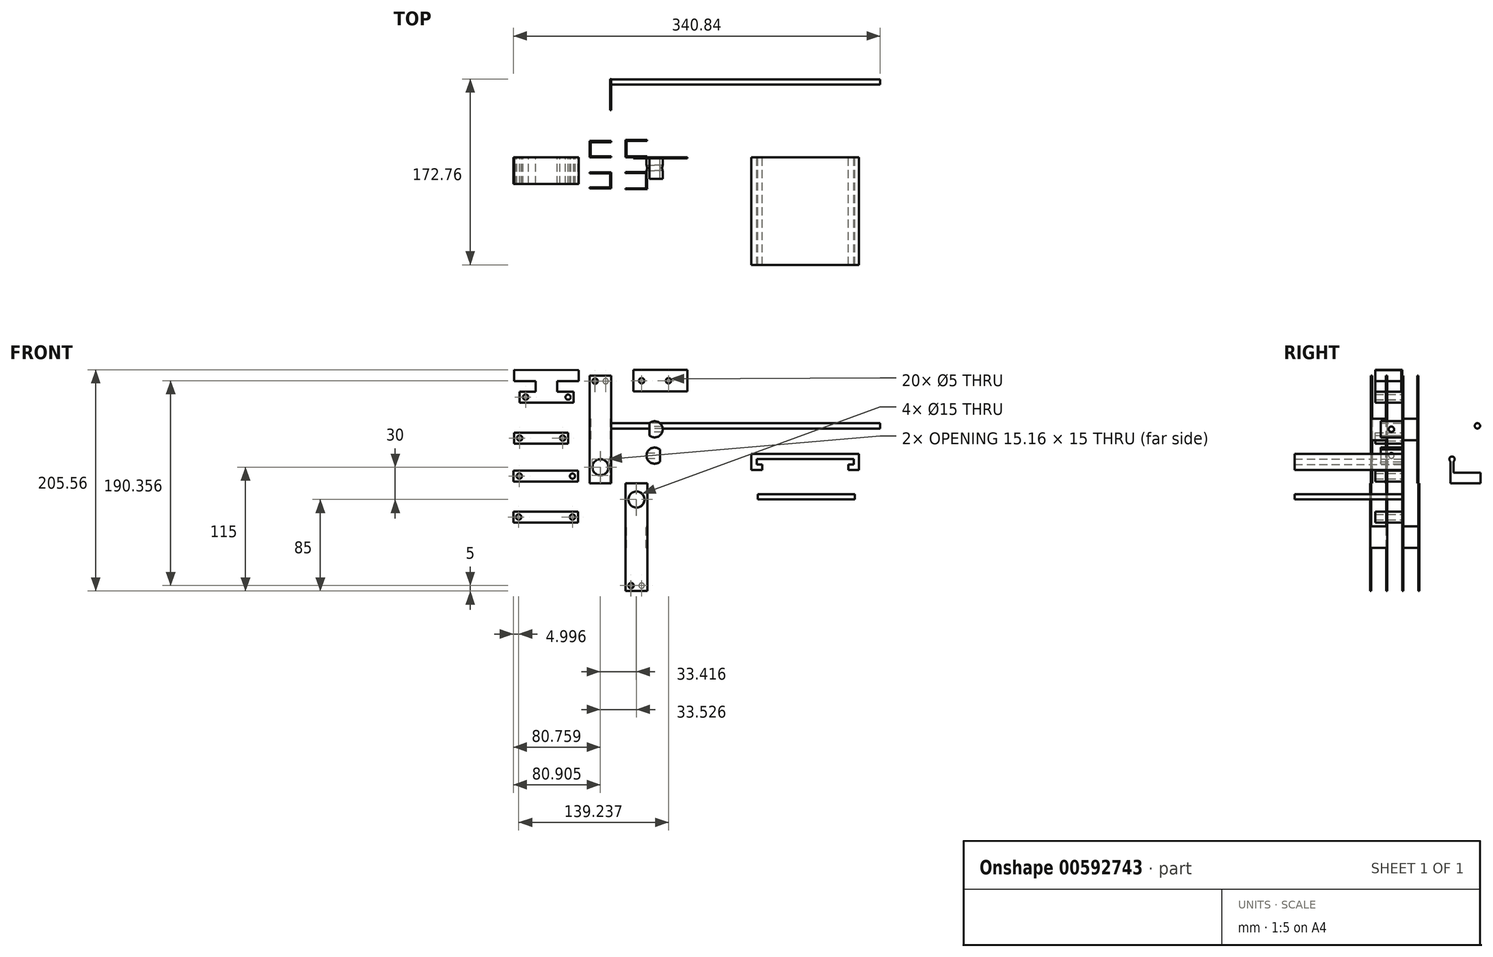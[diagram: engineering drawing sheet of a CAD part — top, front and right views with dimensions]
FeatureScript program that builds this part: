
annotation { "Feature Type Name" : "Feature", "Feature Type Description" : "" }
export const myFeature = defineFeature(function(context is Context, id is Id, definition is map)
    precondition{}
    {
        {
            var Q0;
            Q0=qCreatedBy(makeId("Top.planeOp"),FACE);
            var sketch = newSketch(context, id + "F0", { "sketchPlane" : qUnion([Q0])});
            skLineSegment(sketch, "E0", {"start": v(0, 15) * mm, "end": v(-20, 15) * mm});
            skLineSegment(sketch, "E1", {"start": v(-20, 15) * mm, "end": v(-20, 0) * mm});
            skLineSegment(sketch, "E2", {"start": v(-20, 0) * mm, "end": v(0, 0) * mm});
            skLineSegment(sketch, "E3", {"start": v(0, 0) * mm, "end": v(0, 1) * mm});
            skLineSegment(sketch, "E4", {"start": v(0, 1) * mm, "end": v(-19, 1) * mm});
            skLineSegment(sketch, "E5", {"start": v(-19, 1) * mm, "end": v(-19, 14) * mm});
            skLineSegment(sketch, "E6", {"start": v(-19, 14) * mm, "end": v(0, 14) * mm});
            skLineSegment(sketch, "E7", {"start": v(0, 14) * mm, "end": v(0, 15) * mm});
            skLineSegment(sketch, "E8", {"start": v(33.42, 1) * mm, "end": v(14.42, 1) * mm});
            skLineSegment(sketch, "E9", {"start": v(14.42, 1) * mm, "end": v(14.42, 15) * mm});
            skLineSegment(sketch, "E10", {"start": v(14.42, 15) * mm, "end": v(33.42, 15) * mm});
            skLineSegment(sketch, "E11", {"start": v(33.42, 15) * mm, "end": v(33.42, 16) * mm});
            skLineSegment(sketch, "E12", {"start": v(33.42, 16) * mm, "end": v(13.42, 16) * mm});
            skLineSegment(sketch, "E13", {"start": v(13.42, 16) * mm, "end": v(13.42, 0) * mm});
            skLineSegment(sketch, "E14", {"start": v(13.42, 0) * mm, "end": v(33.42, 0) * mm});
            skLineSegment(sketch, "E15", {"start": v(33.42, 0) * mm, "end": v(33.42, 1) * mm});
            skLineSegment(sketch, "E16", {"start": v(-36.62, -7.13) * mm, "end": v(38.64, -6.85) * mm, "construction": true});
            skLineSegment(sketch, "E17.MirrorCS", {"start": v(-19, 16) * mm, "end": v(0, 16) * mm});
            skLineSegment(sketch, "E18.MirrorCS", {"start": v(-19.95, -14.13) * mm, "end": v(0.05, -13.99) * mm});
            skLineSegment(sketch, "E19.MirrorCS", {"start": v(0.16, -28.99) * mm, "end": v(-19.84, -29.13) * mm});
            skLineSegment(sketch, "E20.MirrorCS", {"start": v(13.47, -13.89) * mm, "end": v(33.47, -13.74) * mm});
            skLineSegment(sketch, "E21.MirrorCS", {"start": v(33.58, -29.74) * mm, "end": v(13.58, -29.89) * mm});
            skLineSegment(sketch, "E22", {"start": v(13.47, -13.89) * mm, "end": v(13.47, -14.89) * mm});
            skLineSegment(sketch, "E23", {"start": v(13.47, -14.89) * mm, "end": v(32.47, -14.75) * mm});
            skLineSegment(sketch, "E24", {"start": v(32.58, -28.75) * mm, "end": v(13.58, -28.89) * mm});
            skLineSegment(sketch, "E25", {"start": v(13.58, -28.89) * mm, "end": v(13.58, -29.89) * mm});
            skLineSegment(sketch, "E26", {"start": v(32.58, -28.75) * mm, "end": v(32.47, -14.75) * mm});
            skLineSegment(sketch, "E27", {"start": v(33.47, -13.74) * mm, "end": v(33.58, -29.74) * mm});
            skLineSegment(sketch, "E28", {"start": v(0.05, -13.99) * mm, "end": v(0.16, -28.99) * mm});
            skLineSegment(sketch, "E29", {"start": v(-19.95, -14.13) * mm, "end": v(-19.94, -15.13) * mm});
            skLineSegment(sketch, "E30", {"start": v(-19.94, -15.13) * mm, "end": v(-0.94, -15) * mm});
            skLineSegment(sketch, "E31", {"start": v(-0.94, -15) * mm, "end": v(-0.85, -28) * mm});
            skLineSegment(sketch, "E32", {"start": v(-0.85, -28) * mm, "end": v(-19.84, -28.13) * mm});
            skLineSegment(sketch, "E33", {"start": v(-19.84, -29.13) * mm, "end": v(-19.84, -28.13) * mm});
            skSolve(sketch);
        }
        {
            var Q0;
            Q0=makeQuery(id+"F0.imprint","IMPRINT",FACE,{"disambiguationData":[TD([[makeQuery(id+"F0.imprint","IMPRINT",EDGE,{"derivedFrom":sQuery(id+"F0.wireOp",EDGE,"E0")}),1.0]])]});
            var Q1;
            Q1=makeQuery(id+"F0.imprint","IMPRINT",FACE,{"disambiguationData":[TD([[makeQuery(id+"F0.imprint","IMPRINT",EDGE,{"derivedFrom":sQuery(id+"F0.wireOp",EDGE,"E19.MirrorCS")}),-1.0]])]});
            extrude(context, id + "F1", {"entities" : qUnion([Q0, Q1]), "depth" : 100 * mm, "offsetDistance" : 25 * mm});
        }
        {
            var Q0;
            Q0=makeQuery(id+"F1.opExtrude","SWEPT_FACE",FACE,{"disambiguationData":[OSD([sQuery(id+"F0.wireOp",EDGE,"E2")])]});
            var sketch = newSketch(context, id + "F2", { "sketchPlane" : qUnion([Q0])});
            skCircle(sketch, "E34", {"center": v(-10, 15) * mm, "radius": 7.5 * mm});
            skPoint(sketch, "E34.centerSnap0", {"position": v(-10, 0) * mm});
            skCircle(sketch, "E35", {"center": v(-5, 95) * mm, "radius": 2.5 * mm});
            skSolve(sketch);
        }
        {
            var Q0;
            Q0=makeQuery(id+"F2.imprint","IMPRINT",FACE,{"disambiguationData":[TD([[makeQuery(id+"F2.imprint","IMPRINT",EDGE,{"derivedFrom":sQuery(id+"F2.wireOp",EDGE,"E34")}),1.0]])]});
            var Q1;
            Q1=makeQuery(id+"F2.imprint","IMPRINT",FACE,{"disambiguationData":[TD([[makeQuery(id+"F2.imprint","IMPRINT",EDGE,{"derivedFrom":sQuery(id+"F2.wireOp",EDGE,"E35")}),1.0]])]});
            extrude(context, id + "F3", {"entities" : qUnion([Q0, Q1]), "operationType" : NewBodyOperationType.REMOVE, "endBound" : BoundingType.THROUGH_ALL, "oppositeDirection" : true, "depth" : 25 * mm, "offsetDistance" : 25 * mm});
        }
        {
            var Q0;
            Q0=makeQuery(id+"F1.opExtrude","SWEPT_FACE",FACE,{"disambiguationData":[OSD([sQuery(id+"F0.wireOp",EDGE,"E1")])]});
            var sketch = newSketch(context, id + "F4", { "sketchPlane" : qUnion([Q0])});
            skPoint(sketch, "E36.centerSnap0", {"position": v(-7.5, 0) * mm});
            skLineSegment(sketch, "E37", {"start": v(-14, 0) * mm, "end": v(-14, 40) * mm});
            skLineSegment(sketch, "E38", {"start": v(-14, 40) * mm, "end": v(-1, 40) * mm});
            skLineSegment(sketch, "E39", {"start": v(-1, 40) * mm, "end": v(-1, 0) * mm});
            skLineSegment(sketch, "E40", {"start": v(-14, 100) * mm, "end": v(-14, 60) * mm});
            skLineSegment(sketch, "E41", {"start": v(-14, 60) * mm, "end": v(-1, 60) * mm});
            skLineSegment(sketch, "E42", {"start": v(-1, 60) * mm, "end": v(-1, 100) * mm});
            skSolve(sketch);
        }
        {
            var Q0;
            {var subQ0=sQuery(id+"F4.wireOp",EDGE,"E37");Q0=makeQuery(id+"F4.imprint","IMPRINT",FACE,{"disambiguationData":[TD([[makeQuery(id+"F4.imprint","IMPRINT",EDGE,{"derivedFrom":subQ0}),-1.0]])]});}
            var Q1;
            {var subQ0=sQuery(id+"F4.wireOp",EDGE,"E40");Q1=makeQuery(id+"F4.imprint","IMPRINT",FACE,{"disambiguationData":[TD([[makeQuery(id+"F4.imprint","IMPRINT",EDGE,{"derivedFrom":subQ0}),1.0]])]});}
            extrude(context, id + "F5", {"entities" : qUnion([Q0, Q1]), "operationType" : NewBodyOperationType.REMOVE, "endBound" : BoundingType.THROUGH_ALL, "oppositeDirection" : true, "depth" : 25 * mm, "offsetDistance" : 25 * mm});
        }
        {
            var Q0;
            Q0=makeQuery(id+"F0.imprint","IMPRINT",FACE,{"disambiguationData":[TD([[makeQuery(id+"F0.imprint","IMPRINT",EDGE,{"derivedFrom":sQuery(id+"F0.wireOp",EDGE,"E8")}),1.0]])]});
            var Q1;
            Q1=makeQuery(id+"F0.imprint","IMPRINT",FACE,{"disambiguationData":[TD([[makeQuery(id+"F0.imprint","IMPRINT",EDGE,{"derivedFrom":sQuery(id+"F0.wireOp",EDGE,"E20.MirrorCS")}),-1.0]])]});
            extrude(context, id + "F6", {"entities" : qUnion([Q0, Q1]), "oppositeDirection" : true, "depth" : 100 * mm, "offsetDistance" : 25 * mm});
        }
        {
            var Q0;
            Q0=makeQuery(id+"F6.opExtrude","SWEPT_FACE",FACE,{"disambiguationData":[OSD([sQuery(id+"F0.wireOp",EDGE,"E14")])]});
            var sketch = newSketch(context, id + "F7", { "sketchPlane" : qUnion([Q0])});
            skCircle(sketch, "E43", {"center": v(23.42, -15) * mm, "radius": 7.5 * mm});
            skPoint(sketch, "E43.centerSnap0", {"position": v(23.42, 0) * mm});
            skCircle(sketch, "E44", {"center": v(28.42, -95) * mm, "radius": 2.5 * mm});
            skSolve(sketch);
        }
        {
            var Q0;
            Q0=makeQuery(id+"F7.imprint","IMPRINT",FACE,{"disambiguationData":[TD([[makeQuery(id+"F7.imprint","IMPRINT",EDGE,{"derivedFrom":sQuery(id+"F7.wireOp",EDGE,"E43")}),1.0]])]});
            var Q1;
            Q1=makeQuery(id+"F7.imprint","IMPRINT",FACE,{"disambiguationData":[TD([[makeQuery(id+"F7.imprint","IMPRINT",EDGE,{"derivedFrom":sQuery(id+"F7.wireOp",EDGE,"E44")}),1.0]])]});
            extrude(context, id + "F8", {"entities" : qUnion([Q0, Q1]), "operationType" : NewBodyOperationType.REMOVE, "endBound" : BoundingType.THROUGH_ALL, "oppositeDirection" : true, "depth" : 25 * mm, "offsetDistance" : 25 * mm});
        }
        {
            var Q0;
            Q0=makeQuery(id+"F6.opExtrude","SWEPT_FACE",FACE,{"disambiguationData":[OSD([sQuery(id+"F0.wireOp",EDGE,"E13")])]});
            var sketch = newSketch(context, id + "F9", { "sketchPlane" : qUnion([Q0])});
            skLineSegment(sketch, "E45", {"start": v(-15, 0) * mm, "end": v(-15, -40) * mm});
            skLineSegment(sketch, "E46", {"start": v(-15, -40) * mm, "end": v(-1, -40) * mm});
            skLineSegment(sketch, "E47", {"start": v(-1, -40) * mm, "end": v(-1, 0) * mm});
            skLineSegment(sketch, "E48", {"start": v(-15, -100) * mm, "end": v(-15, -60) * mm});
            skLineSegment(sketch, "E49", {"start": v(-15, -60) * mm, "end": v(-1, -60) * mm});
            skLineSegment(sketch, "E50", {"start": v(-1, -60) * mm, "end": v(-1, -100) * mm});
            skSolve(sketch);
        }
        {
            var Q0;
            {var subQ0=sQuery(id+"F9.wireOp",EDGE,"E45");Q0=makeQuery(id+"F9.imprint","IMPRINT",FACE,{"disambiguationData":[TD([[makeQuery(id+"F9.imprint","IMPRINT",EDGE,{"derivedFrom":subQ0}),1.0]])]});}
            var Q1;
            {var subQ0=sQuery(id+"F9.wireOp",EDGE,"E48");Q1=makeQuery(id+"F9.imprint","IMPRINT",FACE,{"disambiguationData":[TD([[makeQuery(id+"F9.imprint","IMPRINT",EDGE,{"derivedFrom":subQ0}),-1.0]])]});}
            extrude(context, id + "F10", {"entities" : qUnion([Q0, Q1]), "operationType" : NewBodyOperationType.REMOVE, "endBound" : BoundingType.THROUGH_ALL, "oppositeDirection" : true, "depth" : 25 * mm, "offsetDistance" : 25 * mm});
        }
        {
            var Q0;
            Q0=qCreatedBy(makeId("Front.planeOp"),FACE);
            var sketch = newSketch(context, id + "F11", { "sketchPlane" : qUnion([Q0])});
            skLineSegment(sketch, "E51.bottom", {"start": v(20.9, 105.36) * mm, "end": v(70.9, 105.36) * mm});
            skLineSegment(sketch, "E51.top", {"start": v(20.9, 85.36) * mm, "end": v(70.9, 85.36) * mm});
            skLineSegment(sketch, "E51.left", {"start": v(20.9, 105.36) * mm, "end": v(20.9, 85.36) * mm});
            skLineSegment(sketch, "E51.right", {"start": v(70.9, 105.36) * mm, "end": v(70.9, 85.36) * mm});
            skCircle(sketch, "E52", {"center": v(28.4, 95.36) * mm, "radius": 2.5 * mm});
            skPoint(sketch, "E52.centerSnap0", {"position": v(20.9, 95.36) * mm});
            skCircle(sketch, "E53.MirrorC", {"center": v(53.4, 95.36) * mm, "radius": 2.5 * mm});
            skSolve(sketch);
        }
        {
            var Q0;
            Q0=makeQuery(id+"F11.imprint","IMPRINT",FACE,{"disambiguationData":[TD([[makeQuery(id+"F11.imprint","IMPRINT",EDGE,{"derivedFrom":sQuery(id+"F11.wireOp",EDGE,"E51.bottom")}),-1.0]])]});
            extrude(context, id + "F12", {"entities" : qUnion([Q0]), "depth" : 1 * mm, "offsetDistance" : 25 * mm});
        }
        {
            var Q0;
            Q0=makeQuery(id+"F1.opExtrude","SWEPT_FACE",FACE,{"disambiguationData":[OSD([sQuery(id+"F0.wireOp",EDGE,"E19.MirrorCS")])]});
            var sketch = newSketch(context, id + "F13", { "sketchPlane" : qUnion([Q0])});
            skCircle(sketch, "E54", {"center": v(-15.05, 95) * mm, "radius": 2.5 * mm});
            skCircle(sketch, "E55", {"center": v(-10.05, 15) * mm, "radius": 7.5 * mm});
            skPoint(sketch, "E55.centerSnap0", {"position": v(-10.05, 0) * mm});
            skSolve(sketch);
        }
        {
            var Q0;
            Q0=makeQuery(id+"F13.imprint","IMPRINT",FACE,{"disambiguationData":[TD([[makeQuery(id+"F13.imprint","IMPRINT",EDGE,{"derivedFrom":sQuery(id+"F13.wireOp",EDGE,"E54")}),1.0]])]});
            var Q1;
            Q1=makeQuery(id+"F13.imprint","IMPRINT",FACE,{"disambiguationData":[TD([[makeQuery(id+"F13.imprint","IMPRINT",EDGE,{"derivedFrom":sQuery(id+"F13.wireOp",EDGE,"E55")}),1.0]])]});
            extrude(context, id + "F14", {"entities" : qUnion([Q0, Q1]), "operationType" : NewBodyOperationType.REMOVE, "endBound" : BoundingType.THROUGH_ALL, "oppositeDirection" : true, "depth" : 25 * mm, "offsetDistance" : 25 * mm});
        }
        {
            var Q0;
            Q0=makeQuery(id+"F6.opExtrude","SWEPT_FACE",FACE,{"disambiguationData":[OSD([sQuery(id+"F0.wireOp",EDGE,"E21.MirrorCS")])]});
            var sketch = newSketch(context, id + "F15", { "sketchPlane" : qUnion([Q0])});
            skCircle(sketch, "E56", {"center": v(23.36, -15) * mm, "radius": 7.5 * mm});
            skPoint(sketch, "E56.centerSnap0", {"position": v(23.36, 0) * mm});
            skCircle(sketch, "E57", {"center": v(18.36, -95) * mm, "radius": 2.5 * mm});
            skSolve(sketch);
        }
        {
            var Q0;
            Q0=qSketchRegion(id+"F15",true);
            extrude(context, id + "F16", {"entities" : qUnion([Q0]), "operationType" : NewBodyOperationType.REMOVE, "endBound" : BoundingType.THROUGH_ALL, "oppositeDirection" : true, "depth" : 25 * mm, "offsetDistance" : 25 * mm});
        }
        {
            var Q0;
            Q0=makeQuery(id+"F6.opExtrude","SWEPT_FACE",FACE,{"disambiguationData":[OSD([sQuery(id+"F0.wireOp",EDGE,"E27")])]});
            var sketch = newSketch(context, id + "F17", { "sketchPlane" : qUnion([Q0])});
            skLineSegment(sketch, "E58", {"start": v(-14.99, -40) * mm, "end": v(-28.99, -40) * mm});
            skLineSegment(sketch, "E59", {"start": v(-28.99, -40) * mm, "end": v(-28.99, 0) * mm});
            skLineSegment(sketch, "E60", {"start": v(-14.99, -40) * mm, "end": v(-14.99, 0) * mm});
            skLineSegment(sketch, "E61", {"start": v(-28.99, -100) * mm, "end": v(-28.99, -60) * mm});
            skLineSegment(sketch, "E62", {"start": v(-28.99, -60) * mm, "end": v(-14.99, -60) * mm});
            skLineSegment(sketch, "E63", {"start": v(-14.99, -60) * mm, "end": v(-14.99, -100) * mm});
            skSolve(sketch);
        }
        {
            var Q0;
            Q0=makeQuery(id+"F17.imprint","IMPRINT",FACE,{"disambiguationData":[TD([[makeQuery(id+"F17.imprint","IMPRINT",EDGE,{"derivedFrom":sQuery(id+"F17.wireOp",EDGE,"E58")}),-1.0]])]});
            var Q1;
            {var subQ0=sQuery(id+"F17.wireOp",EDGE,"E61");Q1=makeQuery(id+"F17.imprint","IMPRINT",FACE,{"disambiguationData":[TD([[makeQuery(id+"F17.imprint","IMPRINT",EDGE,{"derivedFrom":subQ0}),-1.0]])]});}
            extrude(context, id + "F18", {"entities" : qUnion([Q0, Q1]), "operationType" : NewBodyOperationType.REMOVE, "endBound" : BoundingType.THROUGH_ALL, "oppositeDirection" : true, "depth" : 25 * mm, "offsetDistance" : 25 * mm});
        }
        {
            var Q0;
            Q0=makeQuery(id+"F1.opExtrude","SWEPT_FACE",FACE,{"disambiguationData":[OSD([sQuery(id+"F0.wireOp",EDGE,"E28")])]});
            var sketch = newSketch(context, id + "F19", { "sketchPlane" : qUnion([Q0])});
            skLineSegment(sketch, "E64", {"start": v(-14.99, 0) * mm, "end": v(-14.99, 40) * mm});
            skLineSegment(sketch, "E65", {"start": v(-14.99, 40) * mm, "end": v(-27.99, 40) * mm});
            skLineSegment(sketch, "E66", {"start": v(-27.99, 40) * mm, "end": v(-27.99, 0) * mm});
            skLineSegment(sketch, "E67", {"start": v(-27.99, 100) * mm, "end": v(-27.99, 60) * mm});
            skLineSegment(sketch, "E68", {"start": v(-27.99, 60) * mm, "end": v(-14.99, 60) * mm});
            skLineSegment(sketch, "E69", {"start": v(-14.99, 60) * mm, "end": v(-14.99, 100) * mm});
            skSolve(sketch);
        }
        {
            var Q0;
            {var subQ0=sQuery(id+"F19.wireOp",EDGE,"E64");Q0=makeQuery(id+"F19.imprint","IMPRINT",FACE,{"disambiguationData":[TD([[makeQuery(id+"F19.imprint","IMPRINT",EDGE,{"derivedFrom":subQ0}),1.0]])]});}
            var Q1;
            {var subQ0=sQuery(id+"F19.wireOp",EDGE,"E67");Q1=makeQuery(id+"F19.imprint","IMPRINT",FACE,{"disambiguationData":[TD([[makeQuery(id+"F19.imprint","IMPRINT",EDGE,{"derivedFrom":subQ0}),1.0]])]});}
            extrude(context, id + "F20", {"entities" : qUnion([Q0, Q1]), "operationType" : NewBodyOperationType.REMOVE, "oppositeDirection" : true, "depth" : 25 * mm, "offsetDistance" : 25 * mm});
        }
        {
            var Q0;
            Q0=qCreatedBy(makeId("Front.planeOp"),FACE);
            var sketch = newSketch(context, id + "F21", { "sketchPlane" : qUnion([Q0])});
            skArc(sketch, "E70", {"start": v(35.49, 44.6) * mm, "mid": v(47.93, 50.24) * mm, "end": v(35.49, 55.88) * mm});
            skArc(sketch, "E71", {"start": v(45.38, 31.4) * mm, "mid": v(32.93, 25.77) * mm, "end": v(45.38, 20.13) * mm});
            skLineSegment(sketch, "E72", {"start": v(35.49, 55.88) * mm, "end": v(35.49, 44.6) * mm});
            skLineSegment(sketch, "E73.trimOffspring", {"start": v(45.38, 31.4) * mm, "end": v(45.38, 20.13) * mm});
            skPoint(sketch, "E74.orphan", {"position": v(40.43, 57.74) * mm});
            skSolve(sketch);
        }
        {
            var Q0;
            Q0=makeQuery(id+"F21.imprint","IMPRINT",FACE,{"disambiguationData":[TD([[makeQuery(id+"F21.imprint","IMPRINT",EDGE,{"derivedFrom":sQuery(id+"F21.wireOp",EDGE,"E70")}),1.0]])]});
            var Q1;
            Q1=makeQuery(id+"F21.imprint","IMPRINT",FACE,{"disambiguationData":[TD([[makeQuery(id+"F21.imprint","IMPRINT",EDGE,{"derivedFrom":sQuery(id+"F21.wireOp",EDGE,"E71")}),1.0]])]});
            extrude(context, id + "F22", {"entities" : qUnion([Q0, Q1]), "depth" : 20 * mm, "offsetDistance" : 25 * mm});
        }
        {
            var Q0;
            Q0=qCreatedBy(makeId("Right.planeOp"),FACE);
            var sketch = newSketch(context, id + "F23", { "sketchPlane" : qUnion([Q0])});
            skCircle(sketch, "E75", {"center": v(69.88, 53.43) * mm, "radius": 2.5 * mm});
            skSolve(sketch);
        }
        {
            var Q0;
            Q0=makeQuery(id+"F23.imprint","IMPRINT",FACE,{"disambiguationData":[TD([[makeQuery(id+"F23.imprint","IMPRINT",EDGE,{"derivedFrom":sQuery(id+"F23.wireOp",EDGE,"E75")}),1.0]])]});
            extrude(context, id + "F24", {"entities" : qUnion([Q0]), "depth" : 250 * mm, "offsetDistance" : 25 * mm});
        }
        {
            var Q0;
            Q0=qCreatedBy(makeId("Front.planeOp"),FACE);
            var sketch = newSketch(context, id + "F25", { "sketchPlane" : qUnion([Q0])});
            skLineSegment(sketch, "E76.top", {"start": v(-84.95, 75.12) * mm, "end": v(-34.95, 75.12) * mm});
            skLineSegment(sketch, "E76.left", {"start": v(-84.95, 85.12) * mm, "end": v(-84.95, 75.12) * mm});
            skLineSegment(sketch, "E76.right", {"start": v(-34.95, 85.12) * mm, "end": v(-34.95, 75.12) * mm});
            skCircle(sketch, "E77", {"center": v(-79.38, 80.12) * mm, "radius": 2.5 * mm});
            skPoint(sketch, "E77.centerSnap0", {"position": v(-84.95, 80.12) * mm});
            skCircle(sketch, "E78", {"center": v(-39.95, 80.12) * mm, "radius": 2.41 * mm});
            skPoint(sketch, "E78.centerSnap0", {"position": v(-34.95, 80.12) * mm});
            skLineSegment(sketch, "E79.MirrorCS", {"start": v(-89.95, 47.06) * mm, "end": v(-39.95, 47.06) * mm});
            skLineSegment(sketch, "E80.MirrorCS", {"start": v(-89.95, 37.06) * mm, "end": v(-89.95, 47.06) * mm});
            skLineSegment(sketch, "E81.MirrorCS", {"start": v(-89.95, 37.06) * mm, "end": v(-39.95, 37.06) * mm});
            skLineSegment(sketch, "E82.MirrorCS", {"start": v(-39.95, 37.06) * mm, "end": v(-39.95, 47.06) * mm});
            skCircle(sketch, "E83", {"center": v(-84.95, 42.06) * mm, "radius": 2.5 * mm});
            skPoint(sketch, "E83.centerSnap0", {"position": v(-89.95, 42.06) * mm});
            skCircle(sketch, "E84", {"center": v(-44.95, 42.06) * mm, "radius": 2.5 * mm});
            skPoint(sketch, "E84.centerSnap0", {"position": v(-39.95, 42.06) * mm});
            skLineSegment(sketch, "E85.bottom", {"start": v(-90.84, 11.74) * mm, "end": v(-30.84, 11.74) * mm});
            skLineSegment(sketch, "E85.top", {"start": v(-90.84, 1.74) * mm, "end": v(-30.84, 1.74) * mm});
            skLineSegment(sketch, "E85.left", {"start": v(-90.84, 11.74) * mm, "end": v(-90.84, 1.74) * mm});
            skLineSegment(sketch, "E85.right", {"start": v(-30.84, 11.74) * mm, "end": v(-30.84, 1.74) * mm});
            skCircle(sketch, "E86", {"center": v(-85.27, 6.74) * mm, "radius": 2.5 * mm});
            skPoint(sketch, "E86.centerSnap0", {"position": v(-90.84, 6.74) * mm});
            skCircle(sketch, "E87", {"center": v(-35.84, 6.74) * mm, "radius": 2.41 * mm});
            skPoint(sketch, "E87.centerSnap0", {"position": v(-30.84, 6.74) * mm});
            skLineSegment(sketch, "E88.MirrorCS", {"start": v(-90.84, -36.32) * mm, "end": v(-90.84, -26.32) * mm});
            skLineSegment(sketch, "E89.MirrorCS", {"start": v(-30.84, -36.32) * mm, "end": v(-30.84, -26.32) * mm});
            skCircle(sketch, "E90", {"center": v(-85.84, -31.32) * mm, "radius": 2.5 * mm});
            skPoint(sketch, "E90.centerSnap0", {"position": v(-90.84, -31.32) * mm});
            skCircle(sketch, "E91", {"center": v(-35.84, -31.32) * mm, "radius": 2.5 * mm});
            skPoint(sketch, "E91.centerSnap0", {"position": v(-30.84, -31.32) * mm});
            skLineSegment(sketch, "E92", {"start": v(-90.84, -26.32) * mm, "end": v(-30.84, -26.32) * mm});
            skLineSegment(sketch, "E93", {"start": v(-90.84, -36.32) * mm, "end": v(-30.84, -36.32) * mm});
            skLineSegment(sketch, "E94", {"start": v(-69.95, 85.12) * mm, "end": v(-69.95, 95.12) * mm});
            skLineSegment(sketch, "E95.MirrorCS", {"start": v(-49.95, 85.12) * mm, "end": v(-49.95, 95.12) * mm});
            skLineSegment(sketch, "E96.MirrorCS", {"start": v(-89.95, 135.12) * mm, "end": v(-39.95, 135.12) * mm});
            skLineSegment(sketch, "E97.MirrorCS", {"start": v(-84.95, 85.12) * mm, "end": v(-69.95, 85.12) * mm});
            skLineSegment(sketch, "E98", {"start": v(-89.95, 95.12) * mm, "end": v(-89.95, 105.56) * mm});
            skLineSegment(sketch, "E99", {"start": v(-29.95, 105.12) * mm, "end": v(-29.95, 95.12) * mm});
            skLineSegment(sketch, "E100.trimOffspring", {"start": v(-49.95, 95.12) * mm, "end": v(-29.95, 95.12) * mm});
            skLineSegment(sketch, "E101", {"start": v(-69.95, 95.12) * mm, "end": v(-89.95, 95.12) * mm});
            skLineSegment(sketch, "E102.trimOffspring", {"start": v(-49.95, 85.12) * mm, "end": v(-34.95, 85.12) * mm});
            skPoint(sketch, "E103.end.orphan", {"position": v(-59.95, 75.12) * mm});
            skPoint(sketch, "E103.start.orphan", {"position": v(-59.95, 85.12) * mm});
            skLineSegment(sketch, "E104", {"start": v(-29.95, 105.12) * mm, "end": v(-89.95, 105.56) * mm});
            skLineSegment(sketch, "E105", {"start": v(-59.95, 75.12) * mm, "end": v(-59.95, 105.34) * mm, "construction": true});
            skSolve(sketch);
        }
        {
            var Q0;
            Q0=makeQuery(id+"F25.imprint","IMPRINT",FACE,{"disambiguationData":[TD([[makeQuery(id+"F25.imprint","IMPRINT",EDGE,{"derivedFrom":sQuery(id+"F25.wireOp",EDGE,"E76.bottom")}),-1.0]])]});
            var Q1;
            {var subQ2=sQuery(id+"F25.wireOp",EDGE,"E80.MirrorCS");Q1=makeQuery(id+"F25.imprint","IMPRINT",FACE,{"disambiguationData":[TD([[makeQuery(id+"F25.imprint","IMPRINT",EDGE,{"derivedFrom":subQ2}),-1.0]])]});}
            var Q2;
            Q2=makeQuery(id+"F25.imprint","IMPRINT",FACE,{"disambiguationData":[TD([[makeQuery(id+"F25.imprint","IMPRINT",EDGE,{"derivedFrom":sQuery(id+"F25.wireOp",EDGE,"E76.top")}),1.0]])]});
            extrude(context, id + "F26", {"entities" : qUnion([Q0, Q1, Q2]), "depth" : 25 * mm, "offsetDistance" : 25 * mm});
        }
        {
            var Q0;
            Q0=makeQuery(id+"F25.imprint","IMPRINT",FACE,{"disambiguationData":[TD([[makeQuery(id+"F25.imprint","IMPRINT",EDGE,{"derivedFrom":sQuery(id+"F25.wireOp",EDGE,"E88.MirrorCS")}),-1.0]])]});
            var Q1;
            Q1=makeQuery(id+"F25.imprint","IMPRINT",FACE,{"disambiguationData":[TD([[makeQuery(id+"F25.imprint","IMPRINT",EDGE,{"derivedFrom":sQuery(id+"F25.wireOp",EDGE,"E85.bottom")}),-1.0]])]});
            extrude(context, id + "F27", {"entities" : qUnion([Q0, Q1]), "depth" : 25 * mm, "offsetDistance" : 25 * mm});
        }
        {
            var Q0;
            Q0=makeQuery(id+"F22.opExtrude","SWEPT_FACE",FACE,{"disambiguationData":[OSD([sQuery(id+"F21.wireOp",EDGE,"E73.trimOffspring")])]});
            var sketch = newSketch(context, id + "F28", { "sketchPlane" : qUnion([Q0])});
            skCircle(sketch, "E106", {"center": v(-10, 25.77) * mm, "radius": 2.5 * mm});
            skPoint(sketch, "E106.centerSnap0", {"position": v(-20, 25.77) * mm});
            skPoint(sketch, "E106.centerSnap1", {"position": v(-10, 31.4) * mm});
            skSolve(sketch);
        }
        {
            var Q0;
            Q0=makeQuery(id+"F28.imprint","IMPRINT",FACE,{"disambiguationData":[TD([[makeQuery(id+"F28.imprint","IMPRINT",EDGE,{"derivedFrom":sQuery(id+"F28.wireOp",EDGE,"E106")}),1.0]])]});
            extrude(context, id + "F29", {"entities" : qUnion([Q0]), "operationType" : NewBodyOperationType.REMOVE, "endBound" : BoundingType.THROUGH_ALL, "oppositeDirection" : true, "depth" : 25 * mm, "offsetDistance" : 25 * mm});
        }
        {
            var Q0;
            Q0=makeQuery(id+"F22.opExtrude","SWEPT_FACE",FACE,{"disambiguationData":[OSD([sQuery(id+"F21.wireOp",EDGE,"E72")])]});
            var sketch = newSketch(context, id + "F30", { "sketchPlane" : qUnion([Q0])});
            skCircle(sketch, "E107", {"center": v(10, 50.24) * mm, "radius": 2.5 * mm});
            skPoint(sketch, "E107.centerSnap0", {"position": v(10, 44.6) * mm});
            skPoint(sketch, "E107.centerSnap1", {"position": v(0, 50.24) * mm});
            skSolve(sketch);
        }
        {
            var Q0;
            Q0=makeQuery(id+"F30.imprint","IMPRINT",FACE,{"disambiguationData":[TD([[makeQuery(id+"F30.imprint","IMPRINT",EDGE,{"derivedFrom":sQuery(id+"F30.wireOp",EDGE,"E107")}),1.0]])]});
            extrude(context, id + "F31", {"entities" : qUnion([Q0]), "operationType" : NewBodyOperationType.REMOVE, "endBound" : BoundingType.THROUGH_ALL, "oppositeDirection" : true, "depth" : 25 * mm, "offsetDistance" : 25 * mm});
        }
        {
            var Q0;
            Q0=qCreatedBy(makeId("Right.planeOp"),FACE);
            var sketch = newSketch(context, id + "F32", { "sketchPlane" : qUnion([Q0])});
            skArc(sketch, "E108", {"start": v(47.76, 20.47) * mm, "mid": v(46.3, 25) * mm, "end": v(44.85, 20.47) * mm});
            skLineSegment(sketch, "E109", {"start": v(47.76, 8.68) * mm, "end": v(47.76, 20.47) * mm});
            skLineSegment(sketch, "E110.MirrorCS", {"start": v(44.85, 8.68) * mm, "end": v(44.85, 20.47) * mm});
            skLineSegment(sketch, "E111", {"start": v(37.92, 27.31) * mm, "end": v(57.96, 27.31) * mm, "construction": true});
            skLineSegment(sketch, "E112", {"start": v(44.85, 8.68) * mm, "end": v(44.85, 0) * mm});
            skLineSegment(sketch, "E113", {"start": v(44.85, 0) * mm, "end": v(47.76, 0) * mm});
            skLineSegment(sketch, "E114", {"start": v(47.76, 0) * mm, "end": v(47.76, 8.68) * mm});
            skArc(sketch, "E115.MirrorCS", {"start": v(47.76, 34.16) * mm, "mid": v(46.3, 29.63) * mm, "end": v(44.85, 34.16) * mm});
            skLineSegment(sketch, "E116.MirrorCS", {"start": v(44.85, 45.94) * mm, "end": v(44.85, 34.16) * mm});
            skLineSegment(sketch, "E117.MirrorCS", {"start": v(47.76, 45.94) * mm, "end": v(47.76, 34.16) * mm});
            skLineSegment(sketch, "E118.MirrorCS", {"start": v(44.85, 45.94) * mm, "end": v(44.85, 54.62) * mm});
            skLineSegment(sketch, "E119.MirrorCS", {"start": v(47.76, 54.62) * mm, "end": v(47.76, 45.94) * mm});
            skLineSegment(sketch, "E120.MirrorCS", {"start": v(44.85, 54.62) * mm, "end": v(47.76, 54.62) * mm});
            skSolve(sketch);
        }
        {
            var Q0;
            Q0=makeQuery(id+"F32.imprint","IMPRINT",FACE,{"disambiguationData":[TD([[makeQuery(id+"F32.imprint","IMPRINT",EDGE,{"derivedFrom":sQuery(id+"F32.wireOp",EDGE,"E108")}),1.0]])]});
            var Q1;
            Q1=makeQuery(id+"F32.imprint","IMPRINT",FACE,{"disambiguationData":[TD([[makeQuery(id+"F32.imprint","IMPRINT",EDGE,{"derivedFrom":sQuery(id+"F32.wireOp",EDGE,"E115.MirrorCS")}),-1.0]])]});
            extrude(context, id + "F33", {"entities" : qUnion([Q0, Q1]), "oppositeDirection" : true, "depth" : 1 * mm, "offsetDistance" : 25 * mm});
        }
        {
            var Q0;
            Q0=makeQuery(id+"F33.opExtrude","SWEPT_FACE",FACE,{"disambiguationData":[OSD([sQuery(id+"F32.wireOp",EDGE,"E109"),sQuery(id+"F32.wireOp",EDGE,"E114")])]});
            var sketch = newSketch(context, id + "F34", { "sketchPlane" : qUnion([Q0])});
            skLineSegment(sketch, "E121", {"start": v(0, 10) * mm, "end": v(1, 10) * mm});
            skLineSegment(sketch, "E122", {"start": v(0.98, 44.62) * mm, "end": v(0, 44.62) * mm});
            skSolve(sketch);
        }
        {
            var Q0;
            {var subQ0=sQuery(id+"F34.wireOp",EDGE,"E121");Q0=makeQuery(id+"F34.imprint","IMPRINT",FACE,{"disambiguationData":[TD([[makeQuery(id+"F34.imprint","IMPRINT",EDGE,{"derivedFrom":subQ0}),-1.0]])]});}
            extrude(context, id + "F35", {"entities" : qUnion([Q0]), "operationType" : NewBodyOperationType.ADD, "depth" : 25 * mm, "offsetDistance" : 25 * mm});
        }
        {
            var Q0;
            Q0=qCreatedBy(makeId("Front.planeOp"),FACE);
            var sketch = newSketch(context, id + "F36", { "sketchPlane" : qUnion([Q0])});
            skLineSegment(sketch, "E123", {"start": v(181.33, -15) * mm, "end": v(136.33, -15) * mm});
            skLineSegment(sketch, "E124", {"start": v(136.33, -15) * mm, "end": v(136.33, -10) * mm});
            skLineSegment(sketch, "E125", {"start": v(136.33, -10) * mm, "end": v(181.33, -10) * mm});
            skLineSegment(sketch, "E126", {"start": v(181.33, -10) * mm, "end": v(181.33, -15) * mm, "construction": true});
            skLineSegment(sketch, "E127.MirrorCS", {"start": v(226.33, -10) * mm, "end": v(181.33, -10) * mm});
            skLineSegment(sketch, "E128.MirrorCS", {"start": v(181.33, -15) * mm, "end": v(226.33, -15) * mm});
            skLineSegment(sketch, "E129.MirrorCS", {"start": v(226.33, -15) * mm, "end": v(226.33, -10) * mm});
            skLineSegment(sketch, "E130", {"start": v(119.38, 8.74) * mm, "end": v(249.77, 8.74) * mm, "construction": true});
            skLineSegment(sketch, "E131.MirrorCS", {"start": v(243.3, 8.74) * mm, "end": v(112.9, 8.74) * mm, "construction": true});
            skLineSegment(sketch, "E132.MirrorCS", {"start": v(180.38, 22.49) * mm, "end": v(180.38, 27.49) * mm, "construction": true});
            skLineSegment(sketch, "E133.MirrorCS", {"start": v(220.38, 12.49) * mm, "end": v(220.38, 17.49) * mm});
            skLineSegment(sketch, "E134.MirrorCS", {"start": v(135.38, 17.49) * mm, "end": v(140.38, 17.49) * mm});
            skLineSegment(sketch, "E135.MirrorCS", {"start": v(140.38, 12.49) * mm, "end": v(140.38, 17.49) * mm});
            skLineSegment(sketch, "E136.MirrorCS", {"start": v(135.38, 22.49) * mm, "end": v(135.38, 17.49) * mm});
            skLineSegment(sketch, "E137.MirrorCS", {"start": v(225.38, 17.49) * mm, "end": v(220.38, 17.49) * mm});
            skLineSegment(sketch, "E138.MirrorCS", {"start": v(225.38, 22.49) * mm, "end": v(225.38, 17.49) * mm});
            skLineSegment(sketch, "E139.MirrorCS", {"start": v(140.38, 12.49) * mm, "end": v(130.38, 12.49) * mm});
            skLineSegment(sketch, "E140.MirrorCS", {"start": v(220.38, 12.49) * mm, "end": v(230.38, 12.49) * mm});
            skLineSegment(sketch, "E141.MirrorCS", {"start": v(230.38, 27.49) * mm, "end": v(230.38, 12.49) * mm});
            skLineSegment(sketch, "E142.MirrorCS", {"start": v(230.38, 27.49) * mm, "end": v(180.38, 27.49) * mm});
            skLineSegment(sketch, "E143.MirrorCS", {"start": v(135.38, 22.49) * mm, "end": v(180.38, 22.49) * mm});
            skLineSegment(sketch, "E144.MirrorCS", {"start": v(225.38, 22.49) * mm, "end": v(180.38, 22.49) * mm});
            skLineSegment(sketch, "E145.MirrorCS", {"start": v(130.38, 27.49) * mm, "end": v(180.38, 27.49) * mm});
            skLineSegment(sketch, "E146.MirrorCS", {"start": v(130.38, 27.49) * mm, "end": v(130.38, 12.49) * mm});
            skSolve(sketch);
        }
        {
            var Q0;
            Q0=makeQuery(id+"F36.imprint","IMPRINT",FACE,{"disambiguationData":[TD([[makeQuery(id+"F36.imprint","IMPRINT",EDGE,{"derivedFrom":sQuery(id+"F36.wireOp",EDGE,"E135.MirrorCS")}),1.0]])]});
            var Q1;
            Q1=makeQuery(id+"F36.imprint","IMPRINT",FACE,{"disambiguationData":[TD([[makeQuery(id+"F36.imprint","IMPRINT",EDGE,{"derivedFrom":sQuery(id+"F36.wireOp",EDGE,"E124")}),-1.0]])]});
            extrude(context, id + "F37", {"entities" : qUnion([Q0, Q1]), "depth" : 100 * mm, "offsetDistance" : 25 * mm});
        }
    });
